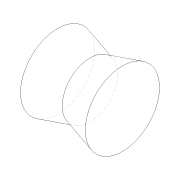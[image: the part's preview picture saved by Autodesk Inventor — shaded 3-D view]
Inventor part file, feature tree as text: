
AUTODESK INVENTOR PART (.ipt)
format: ipt  version: 2020.2 (Build 242310000, 310)  size: 86,016 bytes
history: native  units: mm
features: revolve x1, sketch x1
ambient origin geometry x8: Origin, YZ Plane, XZ Plane, XY Plane, X Axis, Y Axis, Z Axis, Center Point
bodies: Solid1 (feature_tree)
feature tree (2):
  revolve  "Revolution1"  [1 undecoded]
  sketch  "Sketch1"  dims[d0=1.75mm d1=1.0mm d2=0.75mm d3=90.0deg]
note: 1 required parameter value undecoded (feature->parameter linkage not recoverable at this tier; creation-order binding heuristic only, values carry confidence <= 0.55)
